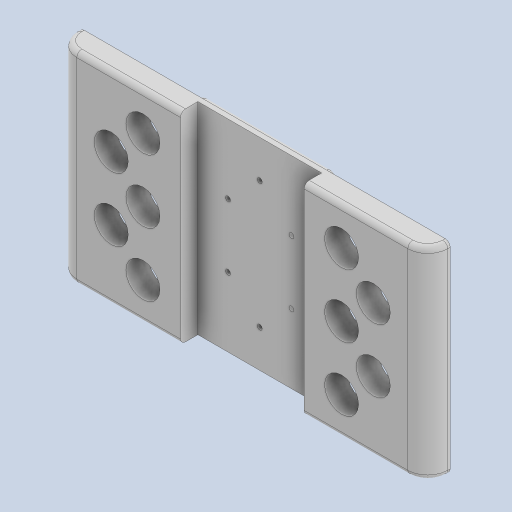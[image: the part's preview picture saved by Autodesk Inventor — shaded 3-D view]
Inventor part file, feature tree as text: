
AUTODESK INVENTOR PART (.ipt)
format: ipt  version: 2024 (Build 280153000, 153)  size: 311,296 bytes
history: native  units: mm
features: projected_geometry x5, extrude x4, sketch x4, fillet x3
ambient origin geometry x8: Origin, YZ Plane, XZ Plane, XY Plane, X Axis, Y Axis, Z Axis, Center Point
bodies: Solid1 (feature_tree)
feature tree (16):
  extrude  "Extrusion1"  Depth=49.5mm
  extrude  "Extrusion2"  Depth=13.607143mm
  extrude  "Extrusion3"  Depth=15.0mm
  extrude  "Extrusion4"  Depth=8.0mm
  fillet  "Fillet1"  Radius=13.607143mm
  fillet  "Fillet2"  [1 undecoded]
  fillet  "Fillet3"  Radius=12.7mm
  sketch  "Sketch1"  dims[d0=49.5mm d1=100.0mm]
  sketch  "Sketch2"  dims[d2=0.0mm d3=13.607143mm]
  projected_geometry  "Projected Loop1"
  sketch  "Sketch3"  dims[d4=13.607143mm d5=15.0mm]
  projected_geometry  "Projected Loop2"
  sketch  "Sketch4"  dims[d6=12.7mm d7=12.7mm d8=13.607143mm d9=0.0mm d10=12.7mm d12=20.0mm d14=25.4mm d15=10.0mm d17=10.0mm d20=0.0mm d21=15.0mm d22=15.0mm d23=80.8mm d24=21.803571mm d25=0.0mm d26=2.0mm d27=0.0mm d28=49.5mm d29=15.0mm d30=15.0mm d31=7.0mm d32=0.0mm d33=2.0mm d34=2.0mm d35=0.0mm d36=12.7mm d37=12.7mm d38=15.0mm d39=2.0mm d40=0.0mm d41=12.7mm d42=12.7mm d43=0.0mm d44=0.0mm d45=5.0mm d46=5.0mm d47=5.0mm d48=5.0mm d49=5.0mm d50=0.0mm d51=37.9mm d52=18.95mm d53=18.95mm d54=2.0mm d55=0.0mm d56=2.0mm d57=2.0mm d58=8.0mm]
  projected_geometry  "Projected Loop3"
  projected_geometry  "Projected Loop4"
  projected_geometry  "Projected Loop5"
note: 1 required parameter value undecoded (feature->parameter linkage not recoverable at this tier; creation-order binding heuristic only, values carry confidence <= 0.55)
